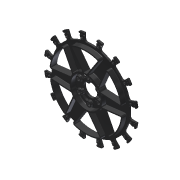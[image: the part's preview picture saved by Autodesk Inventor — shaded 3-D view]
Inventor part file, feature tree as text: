
AUTODESK INVENTOR PART (.ipt)
format: ipt  version: 2013 (Build 170138000, 138)  size: 1,972,736 bytes
history: native  units: in
note: dims shown in document units (in); Inventor stores cm internally (conversion verified against a paired STEP export)
features: fillet x1, other x1, imported_body x1
ambient origin geometry x8: Origin, YZ Plane, XZ Plane, XY Plane, X Axis, Y Axis, Z Axis, Center Point
feature tree (3):
  fillet  "Fillet16"  [1 undecoded]
  other  "217-2613-002 Rev11"
  imported_body  "Base1"
note: 1 required parameter value undecoded (feature->parameter linkage not recoverable at this tier; creation-order binding heuristic only, values carry confidence <= 0.55)
